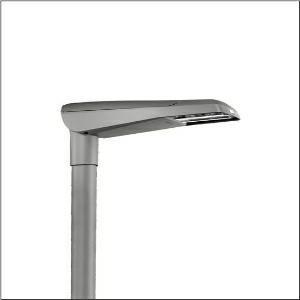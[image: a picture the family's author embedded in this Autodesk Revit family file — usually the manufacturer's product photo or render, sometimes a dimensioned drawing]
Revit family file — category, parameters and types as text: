
# Revit family: streetlight_sl_11_iq_micro___st1_2a_5xc1a61f08ce_98e9
name_source: partatom
category: Lighting Fixtures
units: mm (PartAtom-declared; Revit-internal decimal feet)

## family parameters
Cut with Voids When Loaded = No
Host = Face
Light Source = No
Part Type = Normal
Room Calculation Point = No
Round Connector Dimension = Use Diameter
Shared = No

## types (1)
- --- (1 x LED, 1690 lm, 12.6 W, 2700K)
    Apparent Load = 13 VA
    CIE Flux Codes = 33 71 96 100 100
    Color Rendering = 70
    Color Temperature = 2700K
    Default Elevation = 1800 mm
    Description = Streetlight SL 11 iQ micro, mast luminaire, primary light control with 3 zone facetted reflector, of plastic, silver coated, highly specular, primary optical cover: cover, of PMMA, transparent, light distribution: ST1.2a, light emission: direct distribution, primary light characteristic: asymmetric, installation type: side-entry, post-top, lamps: LED, High Power LED, rated values: 1.690lm | 12,6W | 134,1lm/W (begin service life); end service life: 1.690lm | 12,9W; at 50% lumin. flux: 845lm | 6,8W | 124,3lm/W, colour temperature: 2700K, colour rendering: CRI > 70, light colour: 727, light setting 1 begin service life: 100% | 1.690lm | 12,6W | 134,1lm/W | 2.700K, light setting 1 end service life: 12,9W, further light settings possible, control: optimised constant luminous flux control (CLO 2.0), Desk-Remote (wireless, voltage-free reading and setting of iQ features in the workshop via application-optimized NFC function/RFID function), Light-Fading, Smart-Wire, Night-Set, Lumen-Switch, Temp-Guard, Auto-Match, Street-Remote, with cable H07RN-F 5x 1.5mm², mains connection: 230..240V, AC, 50/60Hz, connection cable pre-assembled, cable length: 5,5m, luminaire housing, of diecast aluminium, powder-coated, Siteco® metallic grey (DB 702S), please order mast flange separately, inclination adjustable without tools: 0°, 5°, 10°, 15° (post-top) | 0°, -5°, -10°, -15° (side-entry), sealing non-destructively replaceable, multi-level sealing system, length: 600mm, width: 174mm, height: 116mm, mast flange for spigot size: 42mm (side-entry): 5XC10008XM4, 60/48mm (side-entry/post-top): 5XC10108XM2, 76/60mm (side-entry/post-top): 5XC10108XM1, equipment: standard, protection rating (complete): IP66, insulation class (complete): insulation class II (safety insulation), certification: CE, ENEC, ENEC+, VDE, impact resistance: IK10, permissible operating ambient temperature for outdoor applications: -25..+50°C, standard-compliant lighting for roads and squares, Environmental Product Declaration (EPD) tested and certified by an independent institute, packaging unit: 1 piece

Light Distribution: ST1.2a
    Height = 116 mm
    Lamp = 1 x LED
    Lamp Light Flux = 1690 lm
    Lamp Power = 12.6 W
    Lamp count = 1
    Length = 600 mm
    Luminous efficacy = 134 lm/W
    Manufacturer = Siteco
    ModVariant = No
    Model = 5XC1A61F08CE
    Number of Poles = 1
    OnlyDefault = Yes
    Power Factor = 1
    Product Name = Streetlight SL 11 iQ micro | ST1.2a
    Product group = mast luminaire | pylon top
    ProductGroupID = 6100
    Protection Class = Protection class II
    Protection Degree = IP 66
    RLX_Detail_Level = 1
    RLX_Emergency_Light_Flux = 0 lm
    RLX_Emergency_Type = 0
    RLX_Emergency_Type_DB = No
    RlxData = <blob elided: 26513 chars, md5=a2dca43a>
    Socket = socket
    Standby Power = 0 W
    System Light Flux = 1690 lm
    System Power = 13 W
    Type Comments = factory setting: luminous flux: 100 % | dim-lin: 254 | 229 mA
    Type Image = l_1006566.jpg
    URL = http://relux.com
    VarID = @adj_017911
    Voltage = 0 V
    Weight = 0.00 kg
    Width = 174 mm

## geometry (parser evidence)
native form markers: Blend x4, Sweep x12
no freeform markers — native parametric forms only
